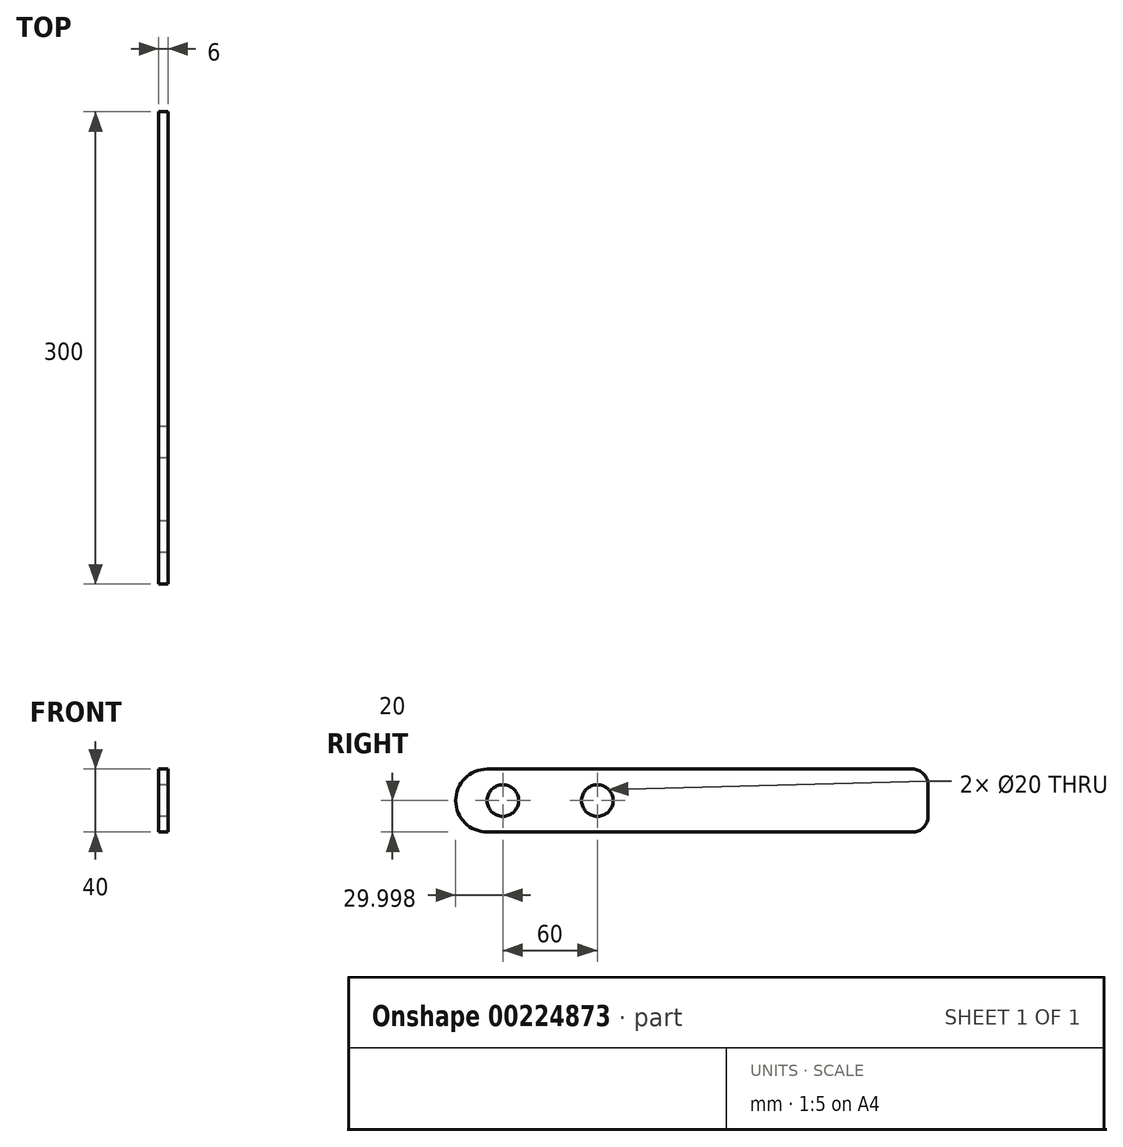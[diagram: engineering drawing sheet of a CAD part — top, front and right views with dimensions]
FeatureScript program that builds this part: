
annotation { "Feature Type Name" : "Feature", "Feature Type Description" : "" }
export const myFeature = defineFeature(function(context is Context, id is Id, definition is map)
    precondition{}
    {
        {
            var Q0;
            Q0=qCreatedBy(makeId("Right.planeOp"),FACE);
            var sketch = newSketch(context, id + "F0", { "sketchPlane" : qUnion([Q0])});
            skLineSegment(sketch, "E0", {"start": v(-161.43, 37) * mm, "end": v(108.57, 37) * mm});
            skLineSegment(sketch, "E1", {"start": v(-181.43, 17) * mm, "end": v(-181.43, 17) * mm});
            skLineSegment(sketch, "E2", {"start": v(-161.43, -3) * mm, "end": v(108.57, -3) * mm});
            skLineSegment(sketch, "E3", {"start": v(118.57, 7) * mm, "end": v(118.57, 27) * mm});
            skPoint(sketch, "E4.visualSharp", {"position": v(118.57, 37) * mm});
            skArc(sketch, "E4.filletArc", {"start": v(118.57, 27) * mm, "mid": v(115.64, 34.08) * mm, "end": v(108.57, 37) * mm});
            skPoint(sketch, "E5.visualSharp", {"position": v(118.57, -3) * mm});
            skArc(sketch, "E5.filletArc", {"start": v(108.57, -3) * mm, "mid": v(115.64, -0.06) * mm, "end": v(118.57, 7) * mm});
            skPoint(sketch, "E6.visualSharp", {"position": v(-181.43, 37) * mm});
            skArc(sketch, "E6.filletArc", {"start": v(-161.43, 37) * mm, "mid": v(-175.57, 31.15) * mm, "end": v(-181.43, 17) * mm});
            skPoint(sketch, "E7.visualSharp", {"position": v(-181.43, -3) * mm});
            skArc(sketch, "E7.filletArc", {"start": v(-181.43, 17) * mm, "mid": v(-175.57, 2.87) * mm, "end": v(-161.43, -3) * mm});
            skLineSegment(sketch, "E8", {"start": v(-181.43, 17) * mm, "end": v(-57.04, 17) * mm, "construction": true});
            skCircle(sketch, "E9", {"center": v(-151.43, 17) * mm, "radius": 10 * mm});
            skCircle(sketch, "E10", {"center": v(-91.43, 17) * mm, "radius": 10 * mm});
            skSolve(sketch);
        }
        {
            var Q0;
            Q0 = qSketchRegion(id + "F0", true);
            extrude(context, id + "F1", {"entities" : qUnion([Q0]), "depth" : 6 * mm});
        }
    });
